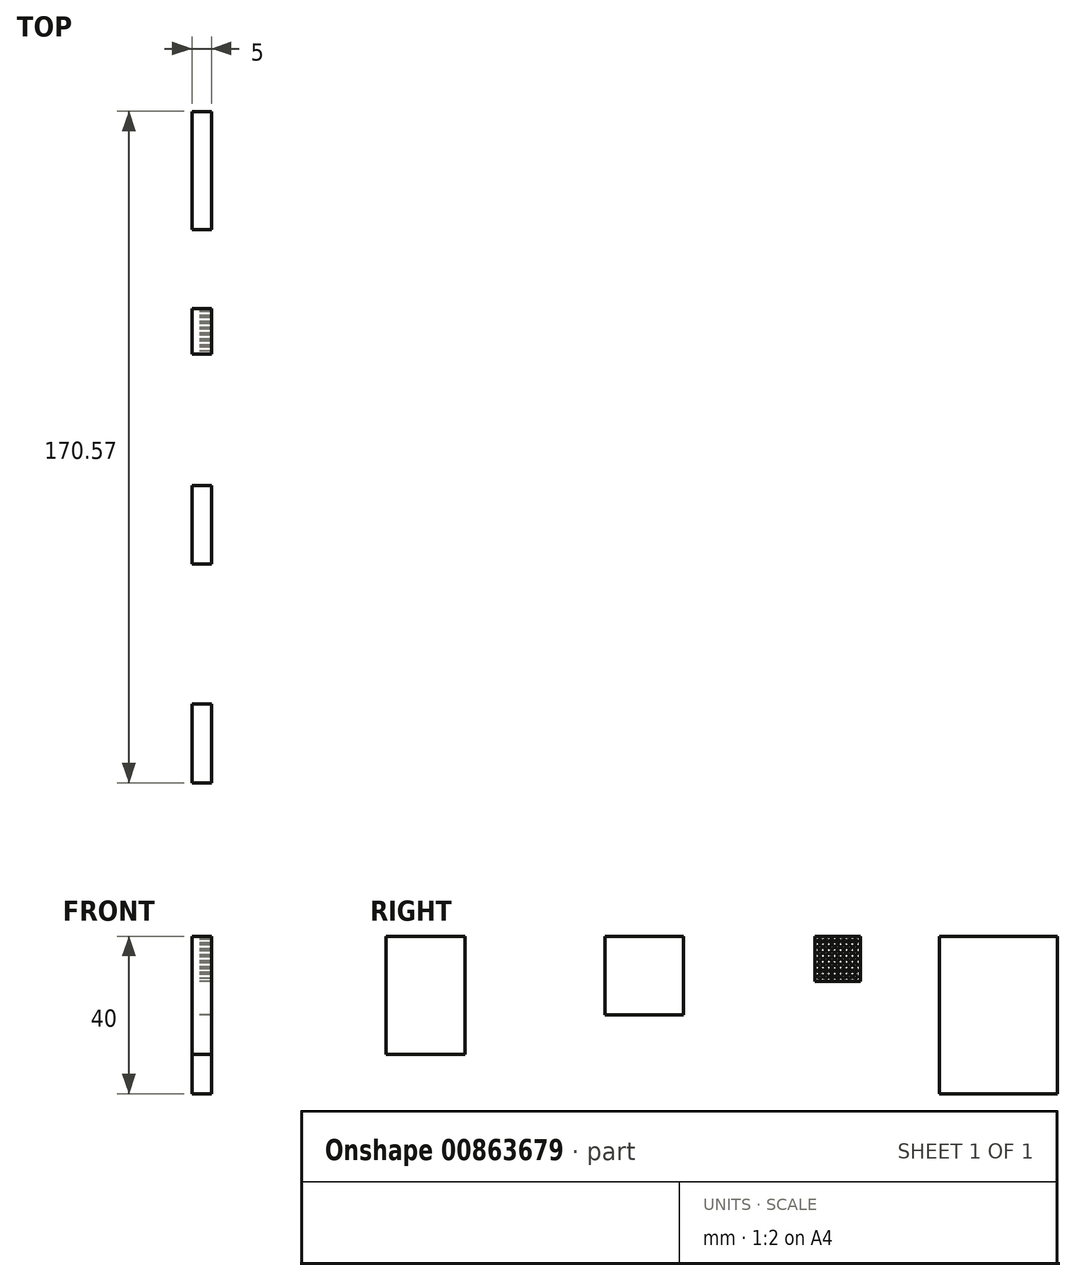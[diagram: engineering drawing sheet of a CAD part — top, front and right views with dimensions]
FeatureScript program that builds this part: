
annotation { "Feature Type Name" : "Feature", "Feature Type Description" : "" }
export const myFeature = defineFeature(function(context is Context, id is Id, definition is map)
    precondition{}
    {
        {
            var Q0;
            Q0=qCreatedBy(makeId("Right.planeOp"),FACE);
            var sketch = newSketch(context, id + "F0", { "sketchPlane" : qUnion([Q0])});
            skLineSegment(sketch, "E0.bottom", {"start": v(0, 0) * mm, "end": v(11.5, 0) * mm});
            skLineSegment(sketch, "E0.top", {"start": v(0, -11.5) * mm, "end": v(11.5, -11.5) * mm});
            skLineSegment(sketch, "E0.left", {"start": v(0, 0) * mm, "end": v(0, -11.5) * mm});
            skLineSegment(sketch, "E1.bottom", {"start": v(31.62, 0) * mm, "end": v(61.62, 0) * mm});
            skLineSegment(sketch, "E1.top", {"start": v(31.62, -40) * mm, "end": v(61.62, -40) * mm});
            skLineSegment(sketch, "E1.left", {"start": v(31.62, 0) * mm, "end": v(31.62, -40) * mm});
            skLineSegment(sketch, "E1.right", {"start": v(61.62, 0) * mm, "end": v(61.62, -40) * mm});
            skLineSegment(sketch, "E2.bottom", {"start": v(-53.4, 0) * mm, "end": v(-33.4, 0) * mm});
            skLineSegment(sketch, "E2.top", {"start": v(-53.4, -20) * mm, "end": v(-33.4, -20) * mm});
            skLineSegment(sketch, "E2.left", {"start": v(-53.4, 0) * mm, "end": v(-53.4, -20) * mm});
            skLineSegment(sketch, "E2.right", {"start": v(-33.4, 0) * mm, "end": v(-33.4, -20) * mm});
            skLineSegment(sketch, "E3.bottom", {"start": v(-88.95, 0) * mm, "end": v(-108.95, 0) * mm});
            skLineSegment(sketch, "E3.top", {"start": v(-88.95, -30) * mm, "end": v(-108.95, -30) * mm});
            skLineSegment(sketch, "E3.left", {"start": v(-88.95, 0) * mm, "end": v(-88.95, -30) * mm});
            skLineSegment(sketch, "E3.right", {"start": v(-108.95, 0) * mm, "end": v(-108.95, -30) * mm});
            skCircle(sketch, "E4", {"center": v(5.75, -5.75) * mm, "radius": 0.5 * mm});
            skLineSegment(sketch, "E5", {"start": v(11.5, 0) * mm, "end": v(11.5, -11.5) * mm});
            skCircle(sketch, "E6", {"center": v(5.75, -4.25) * mm, "radius": 0.5 * mm});
            skCircle(sketch, "E7", {"center": v(5.75, -2.75) * mm, "radius": 0.5 * mm});
            skCircle(sketch, "E8", {"center": v(4.25, -5.75) * mm, "radius": 0.5 * mm});
            skCircle(sketch, "E9", {"center": v(5.75, -1.25) * mm, "radius": 0.5 * mm});
            skCircle(sketch, "E10", {"center": v(4.25, -4.25) * mm, "radius": 0.5 * mm});
            skCircle(sketch, "E11", {"center": v(4.25, -2.75) * mm, "radius": 0.5 * mm});
            skCircle(sketch, "E12", {"center": v(4.25, -1.25) * mm, "radius": 0.5 * mm});
            skCircle(sketch, "E13", {"center": v(2.75, -5.75) * mm, "radius": 0.5 * mm});
            skCircle(sketch, "E14", {"center": v(2.75, -4.25) * mm, "radius": 0.5 * mm});
            skCircle(sketch, "E15", {"center": v(2.75, -2.75) * mm, "radius": 0.5 * mm});
            skCircle(sketch, "E16", {"center": v(2.75, -1.25) * mm, "radius": 0.5 * mm});
            skCircle(sketch, "E17", {"center": v(1.25, -5.75) * mm, "radius": 0.5 * mm});
            skCircle(sketch, "E18", {"center": v(1.25, -4.25) * mm, "radius": 0.5 * mm});
            skCircle(sketch, "E19", {"center": v(1.25, -2.75) * mm, "radius": 0.5 * mm});
            skCircle(sketch, "E20", {"center": v(1.25, -1.25) * mm, "radius": 0.5 * mm});
            skCircle(sketch, "E21.MirrorC", {"center": v(7.25, -1.25) * mm, "radius": 0.5 * mm});
            skCircle(sketch, "E22.MirrorC", {"center": v(7.25, -2.75) * mm, "radius": 0.5 * mm});
            skCircle(sketch, "E23.MirrorC", {"center": v(7.25, -4.25) * mm, "radius": 0.5 * mm});
            skCircle(sketch, "E24.MirrorC", {"center": v(7.25, -5.75) * mm, "radius": 0.5 * mm});
            skCircle(sketch, "E25.MirrorC", {"center": v(8.75, -5.75) * mm, "radius": 0.5 * mm});
            skCircle(sketch, "E26.MirrorC", {"center": v(8.75, -4.25) * mm, "radius": 0.5 * mm});
            skCircle(sketch, "E27.MirrorC", {"center": v(8.75, -2.75) * mm, "radius": 0.5 * mm});
            skCircle(sketch, "E28.MirrorC", {"center": v(8.75, -1.25) * mm, "radius": 0.5 * mm});
            skCircle(sketch, "E29.MirrorC", {"center": v(10.25, -1.25) * mm, "radius": 0.5 * mm});
            skCircle(sketch, "E30.MirrorC", {"center": v(10.25, -2.75) * mm, "radius": 0.5 * mm});
            skCircle(sketch, "E31.MirrorC", {"center": v(10.25, -4.25) * mm, "radius": 0.5 * mm});
            skCircle(sketch, "E32.MirrorC", {"center": v(10.25, -5.75) * mm, "radius": 0.5 * mm});
            skCircle(sketch, "E33.MirrorC", {"center": v(1.25, -7.25) * mm, "radius": 0.5 * mm});
            skCircle(sketch, "E34.MirrorC", {"center": v(2.75, -7.25) * mm, "radius": 0.5 * mm});
            skCircle(sketch, "E35.MirrorC", {"center": v(4.25, -7.25) * mm, "radius": 0.5 * mm});
            skCircle(sketch, "E36.MirrorC", {"center": v(4.25, -8.75) * mm, "radius": 0.5 * mm});
            skCircle(sketch, "E37.MirrorC", {"center": v(2.75, -8.75) * mm, "radius": 0.5 * mm});
            skCircle(sketch, "E38.MirrorC", {"center": v(1.25, -8.75) * mm, "radius": 0.5 * mm});
            skCircle(sketch, "E39.MirrorC", {"center": v(1.25, -10.25) * mm, "radius": 0.5 * mm});
            skCircle(sketch, "E40.MirrorC", {"center": v(2.75, -10.25) * mm, "radius": 0.5 * mm});
            skCircle(sketch, "E41.MirrorC", {"center": v(4.25, -10.25) * mm, "radius": 0.5 * mm});
            skCircle(sketch, "E42.MirrorC", {"center": v(5.75, -10.25) * mm, "radius": 0.5 * mm});
            skCircle(sketch, "E43.MirrorC", {"center": v(5.75, -8.75) * mm, "radius": 0.5 * mm});
            skCircle(sketch, "E44.MirrorC", {"center": v(5.75, -7.25) * mm, "radius": 0.5 * mm});
            skCircle(sketch, "E45.MirrorC", {"center": v(7.25, -7.25) * mm, "radius": 0.5 * mm});
            skCircle(sketch, "E46.MirrorC", {"center": v(7.25, -8.75) * mm, "radius": 0.5 * mm});
            skCircle(sketch, "E47.MirrorC", {"center": v(7.25, -10.25) * mm, "radius": 0.5 * mm});
            skCircle(sketch, "E48.MirrorC", {"center": v(8.75, -10.25) * mm, "radius": 0.5 * mm});
            skCircle(sketch, "E49.MirrorC", {"center": v(8.75, -8.75) * mm, "radius": 0.5 * mm});
            skCircle(sketch, "E50.MirrorC", {"center": v(8.75, -7.25) * mm, "radius": 0.5 * mm});
            skCircle(sketch, "E51.MirrorC", {"center": v(10.25, -7.25) * mm, "radius": 0.5 * mm});
            skCircle(sketch, "E52.MirrorC", {"center": v(10.25, -8.75) * mm, "radius": 0.5 * mm});
            skCircle(sketch, "E53.MirrorC", {"center": v(10.25, -10.25) * mm, "radius": 0.5 * mm});
            skSolve(sketch);
        }
        {
            var Q0;
            Q0=makeQuery(id+"F0.imprint","IMPRINT",FACE,{"disambiguationData":[TD([[makeQuery(id+"F0.imprint","IMPRINT",EDGE,{"derivedFrom":sQuery(id+"F0.wireOp",EDGE,"E0.bottom")}),-1.0]])]});
            var Q1;
            Q1=makeQuery(id+"F0.imprint","IMPRINT",FACE,{"disambiguationData":[TD([[makeQuery(id+"F0.imprint","IMPRINT",EDGE,{"derivedFrom":sQuery(id+"F0.wireOp",EDGE,"E1.bottom")}),-1.0]])]});
            var Q2;
            Q2=makeQuery(id+"F0.imprint","IMPRINT",FACE,{"disambiguationData":[TD([[makeQuery(id+"F0.imprint","IMPRINT",EDGE,{"derivedFrom":sQuery(id+"F0.wireOp",EDGE,"E3.bottom")}),1.0]])]});
            var Q3;
            Q3=makeQuery(id+"F0.imprint","IMPRINT",FACE,{"disambiguationData":[TD([[makeQuery(id+"F0.imprint","IMPRINT",EDGE,{"derivedFrom":sQuery(id+"F0.wireOp",EDGE,"E2.bottom")}),-1.0]])]});
            extrude(context, id + "F1", {"entities" : qUnion([Q0, Q1, Q2, Q3]), "depth" : 5 * mm, "offsetDistance" : 25 * mm});
        }
    });
